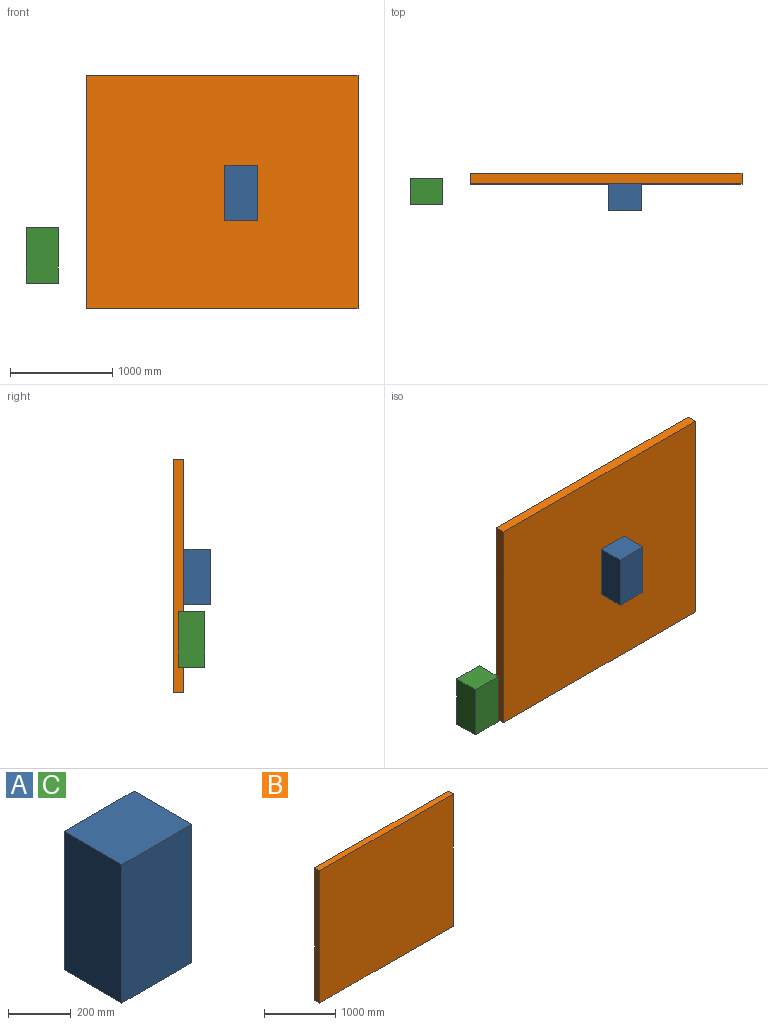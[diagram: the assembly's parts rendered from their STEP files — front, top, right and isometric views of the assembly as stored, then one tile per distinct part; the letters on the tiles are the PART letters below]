
ASSEMBLY  parts=3 mates=3
PART A: 14 faces, bbox 315x260x540 mm
  f0: plane 540x260mm, normal (-1,0,0), area 140400mm2, adj f1,f3,f4,f5
  f1: plane 315x260mm, normal (0,0,-1), area 81900mm2, adj f0,f2,f4,f5
  f2: plane 540x260mm, normal (1,0,0), area 140400mm2, adj f1,f3,f4,f5
  f3: plane 315x260mm, normal (0,0,1), area 81900mm2, adj f0,f2,f4,f5
  f4: plane 540x315mm, normal (0,-1,0), area 170100mm2, adj f0,f1,f2,f3
  f5: plane 540x315mm, normal (0,1,0), area 169845.5mm2, adj f0,f1,f2,f3,f6,f8,f10,f12
  f6: cylinder r=4.5mm len=25mm, axis (0,1,0), area 706.9mm2, adj f5,f7
  f7: plane 9x9mm, normal (0,1,0), area 63.6mm2, adj f6
  f8: cylinder r=4.5mm len=25mm, axis (0,1,0), area 706.9mm2, adj f5,f9
  f9: plane 9x9mm, normal (0,1,0), area 63.6mm2, adj f8
  f10: cylinder r=4.5mm len=25mm, axis (0,1,0), area 706.9mm2, adj f5,f11
  f11: plane 9x9mm, normal (0,1,0), area 63.6mm2, adj f10
  f12: cylinder r=4.5mm len=25mm, axis (0,1,0), area 706.9mm2, adj f5,f13
  f13: plane 9x9mm, normal (0,1,0), area 63.6mm2, adj f12
PART B: 6 faces, bbox 2650x100x2280 mm
  f0: plane 2280x100mm, normal (-1,0,0), area 228000mm2, adj f1,f3,f4,f5
  f1: plane 2650x100mm, normal (0,0,-1), area 265000mm2, adj f0,f2,f4,f5
  f2: plane 2280x100mm, normal (1,0,0), area 228000mm2, adj f1,f3,f4,f5
  f3: plane 2650x100mm, normal (0,0,1), area 265000mm2, adj f0,f2,f4,f5
  f4: plane 2650x2280mm, normal (0,-1,0), area 6042000mm2, adj f0,f1,f2,f3
  f5: plane 2650x2280mm, normal (0,1,0), area 6042000mm2, adj f0,f1,f2,f3
PART C: same geometry as A
PLACE A t=(1922.34,-237.89,761.49)mm
PLACE B t=(571.21,-137.89,-97.56)mm
PLACE C t=(-20.39,-181.51,153.09)mm
MATE parallel A.f5 <-> B.f4  axis (0,1,0) through (2079.84,-237.89,1031.26)mm
MATE parallel A.f2 <-> B.f2  axis (1,0,0) through (2237.34,-367.89,1031.49)mm
MATE planar B.f4 <-> A.f5  axis (0,-1,0) through (1896.21,-237.89,1042.44)mm
